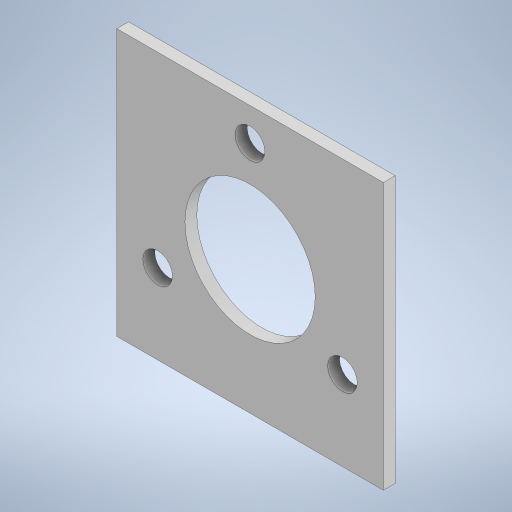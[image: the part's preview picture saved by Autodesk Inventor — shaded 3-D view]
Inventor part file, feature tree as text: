
AUTODESK INVENTOR PART (.ipt)
format: ipt  version: 2024 (Build 280153000, 153)  size: 240,128 bytes
history: native  units: in
note: dims shown in document units (in); Inventor stores cm internally (conversion verified against a paired STEP export)
features: extrude x1, sketch x1
ambient origin geometry x8: Origin, YZ Plane, XZ Plane, XY Plane, X Axis, Y Axis, Z Axis, Center Point
bodies: Body1 (feature_tree)
feature tree (2):
  extrude  "Extrusion2"  Depth=1.7717in
  sketch  "Sketch1"  dims[d0=1.7717in d1=1.7717in d2=0.8661in d3=0.6693in d4=0.6142in d5=120.0deg d6=0.6142in d7=120.0deg d8=0.1969in d9=0.1969in d10=0.1969in d16=0.0787in d17=0.0in d11=0.0197in d12=0.0344in d13=0.0197in d14=0.0344in]
